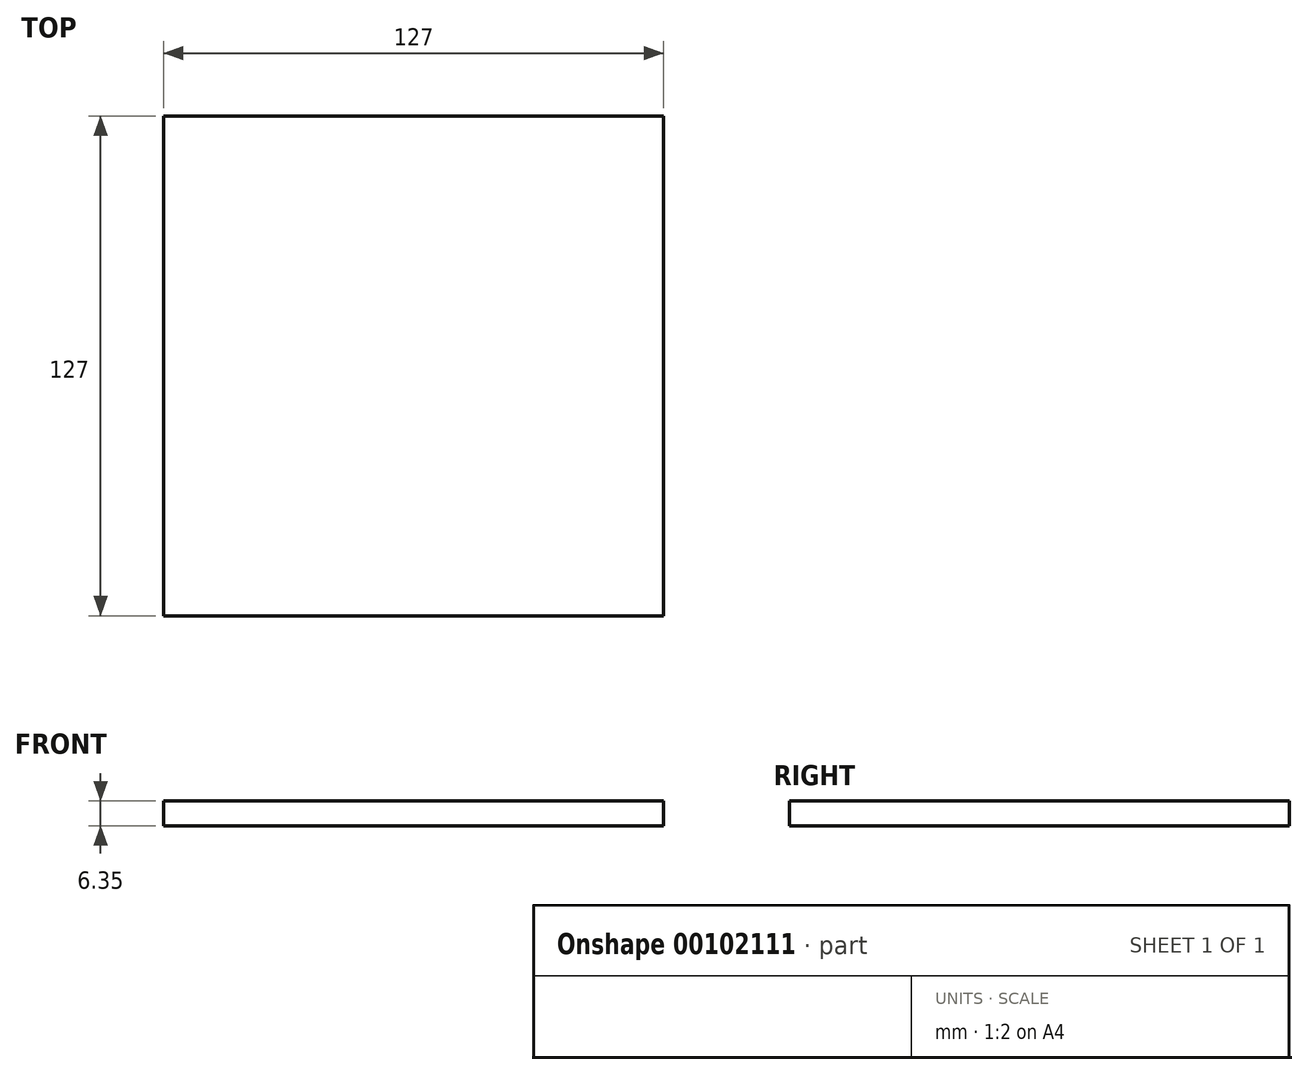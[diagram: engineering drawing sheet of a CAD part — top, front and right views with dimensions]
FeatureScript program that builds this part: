
annotation { "Feature Type Name" : "Feature", "Feature Type Description" : "" }
export const myFeature = defineFeature(function(context is Context, id is Id, definition is map)
    precondition{}
    {
        {
            var Q0;
            Q0=qCreatedBy(makeId("Top.planeOp"),FACE);
            var sketch = newSketch(context, id + "F0", { "sketchPlane" : qUnion([Q0])});
            skLineSegment(sketch, "E0.bottom", {"start": v(70.47, -46.27) * mm, "end": v(-56.53, -46.27) * mm});
            skLineSegment(sketch, "E0.top", {"start": v(70.47, 80.73) * mm, "end": v(-56.53, 80.73) * mm});
            skLineSegment(sketch, "E0.left", {"start": v(70.47, -46.27) * mm, "end": v(70.47, 80.73) * mm});
            skLineSegment(sketch, "E0.right", {"start": v(-56.53, -46.27) * mm, "end": v(-56.53, 80.73) * mm});
            skSolve(sketch);
        }
        {
            var Q0;
            Q0=makeQuery(id+"F0.imprint","IMPRINT",FACE,{"disambiguationData":[TD([[makeQuery(id+"F0.imprint","IMPRINT",EDGE,{"derivedFrom":sQuery(id+"F0.wireOp",EDGE,"E0.bottom")}),-1.0]])]});
            extrude(context, id + "F1", {"entities" : qUnion([Q0]), "depth" : 6.35 * mm});
        }
        {
            var Q0;
            Q0=makeQuery(id+"F1.opExtrude","SWEPT_FACE",FACE,{"disambiguationData":[OSD([sQuery(id+"F0.wireOp",EDGE,"E0.bottom")])]});
            var sketch = newSketch(context, id + "F2", { "sketchPlane" : qUnion([Q0])});
            skCircle(sketch, "E1", {"center": v(-6.88, 18.15) * mm, "radius": 6.35 * mm});
            skCircle(sketch, "E2", {"center": v(52.55, 18.41) * mm, "radius": 3.18 * mm});
            skSolve(sketch);
        }
        {
            var Q0;
            Q0 = qSketchRegion(id + "F2", true);
            extrude(context, id + "F3", {"entities" : qUnion([Q0]), "operationType" : NewBodyOperationType.REMOVE, "oppositeDirection" : true, "depth" : 254 * mm});
        }
    });
